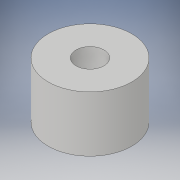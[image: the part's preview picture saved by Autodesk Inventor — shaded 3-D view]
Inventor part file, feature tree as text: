
AUTODESK INVENTOR PART (.ipt)
format: ipt  version: 2019 (Build 230136000, 136)  size: 98,304 bytes
history: native  units: mm
features: other x1, extrude x1, sketch x1
ambient origin geometry x8: Origin, YZ Plane, XZ Plane, XY Plane, X Axis, Y Axis, Z Axis, Center Point
bodies: Body1 (feature_tree)
feature tree (3):
  other  "ソリッド1"
  extrude  "押し出し1"  Depth=30.0mm
  sketch  "スケッチ1"
